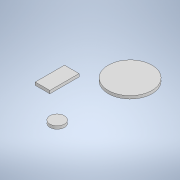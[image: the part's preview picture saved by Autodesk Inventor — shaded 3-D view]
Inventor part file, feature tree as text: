
AUTODESK INVENTOR PART (.ipt)
format: ipt  version: 2020.2 (Build 242310000, 310)  size: 109,568 bytes
history: native  units: mm
features: extrude x1, sketch x1
ambient origin geometry x8: Origin, YZ Plane, XZ Plane, XY Plane, X Axis, Y Axis, Z Axis, Center Point
bodies: Solid1 (feature_tree)
feature tree (2):
  extrude  "Extrusion1"  Depth=100.0mm
  sketch  "Sketch1"  dims[d0=5000.0mm d1=5000.0mm d2=500.0mm d3=1500.0mm d4=500.0mm d5=1000.0mm d6=100.0mm d7=0.0mm]
